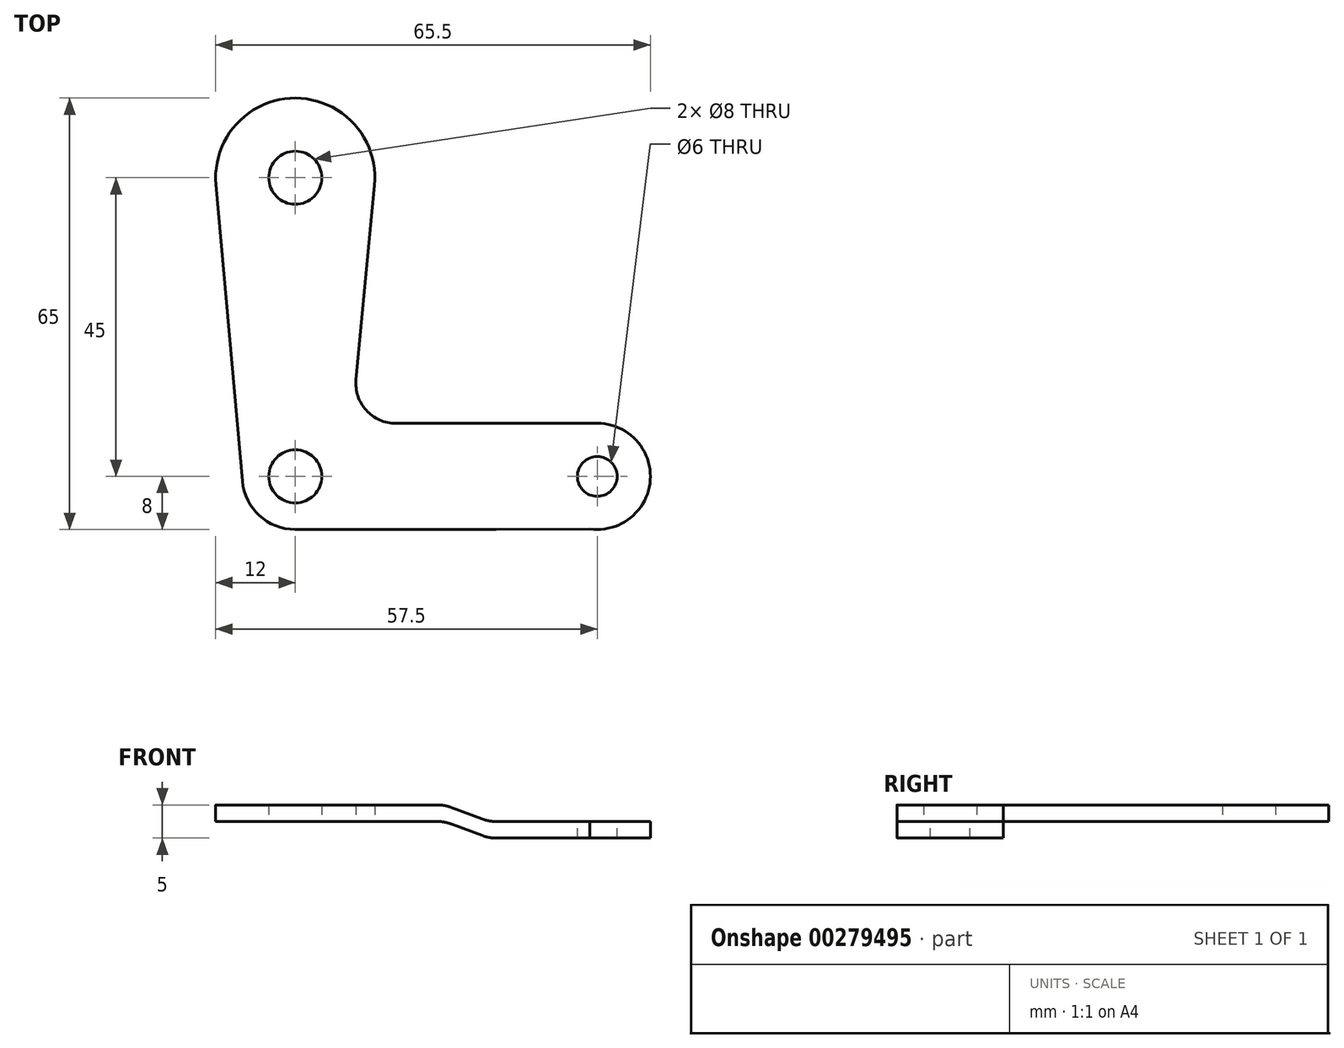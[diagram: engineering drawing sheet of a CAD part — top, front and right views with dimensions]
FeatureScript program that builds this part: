
annotation { "Feature Type Name" : "Feature", "Feature Type Description" : "" }
export const myFeature = defineFeature(function(context is Context, id is Id, definition is map)
    precondition{}
    {
        {
            var Q0;
            Q0=qCreatedBy(makeId("Top.planeOp"),FACE);
            var sketch = newSketch(context, id + "F0", { "sketchPlane" : qUnion([Q0])});
            skCircle(sketch, "E0", {"center": v(0, 0) * mm, "radius": 4 * mm});
            skCircle(sketch, "E1", {"center": v(0, 45) * mm, "radius": 4 * mm});
            skArc(sketch, "E2", {"start": v(11.95, 43.86) * mm, "mid": v(0.04, 57) * mm, "end": v(-11.95, 43.93) * mm});
            skArc(sketch, "E3", {"start": v(-7.97, -0.71) * mm, "mid": v(-5.4, -5.9) * mm, "end": v(0, -8) * mm});
            skLineSegment(sketch, "E4", {"start": v(-11.95, 43.93) * mm, "end": v(-7.97, -0.71) * mm});
            skLineSegment(sketch, "E5", {"start": v(0, -8) * mm, "end": v(22.5, -8) * mm});
            skLineSegment(sketch, "E6", {"start": v(11.95, 43.86) * mm, "end": v(9.16, 14.57) * mm});
            skLineSegment(sketch, "E7", {"start": v(15.13, 8) * mm, "end": v(22.5, 8) * mm});
            skPoint(sketch, "E8.visualSharp", {"position": v(8.53, 8) * mm});
            skArc(sketch, "E8.filletArc", {"start": v(9.16, 14.57) * mm, "mid": v(10.7, 9.96) * mm, "end": v(15.13, 8) * mm});
            skLineSegment(sketch, "E9", {"start": v(22.5, 8) * mm, "end": v(22.5, -8) * mm});
            skSolve(sketch);
        }
        {
            var Q0;
            Q0=qSketchRegion(id+"F0",true);
            extrude(context, id + "F1", {"entities" : qUnion([Q0]), "oppositeDirection" : true, "depth" : 2.5 * mm});
        }
        {
            var Q0;
            Q0=makeQuery(id+"F1.opExtrude","CAP_FACE",FACE,{"disambiguationData":[OSD([sQuery(id+"F0.wireOp",EDGE,"E0"),sQuery(id+"F0.wireOp",EDGE,"E1"),sQuery(id+"F0.wireOp",EDGE,"E2"),sQuery(id+"F0.wireOp",EDGE,"E3"),sQuery(id+"F0.wireOp",EDGE,"E4"),sQuery(id+"F0.wireOp",EDGE,"E5"),sQuery(id+"F0.wireOp",EDGE,"E6"),sQuery(id+"F0.wireOp",EDGE,"E7"),sQuery(id+"F0.wireOp",EDGE,"E8.filletArc"),sQuery(id+"F0.wireOp",EDGE,"E9")])],"isStart":false});
            cPlane(context, id + "F2", {"entities" : qUnion([Q0]), "cplaneType" : CPlaneType.OFFSET, "offset" : 2.5 * mm, "oppositeDirection" : true, "width" : 150 * mm, "height" : 150 * mm});
        }
        {
            var Q0;
            Q0=qCreatedBy(id+"F2.planeOp",FACE);
            var sketch = newSketch(context, id + "F3", { "sketchPlane" : qUnion([Q0])});
            skCircle(sketch, "E10.0", {"center": v(0, 0) * mm, "radius": 4 * mm, "construction": true});
            skLineSegment(sketch, "E11.0", {"start": v(22.5, -8) * mm, "end": v(22.5, 8) * mm, "construction": true});
            skCircle(sketch, "E12", {"center": v(45.5, 0) * mm, "radius": 3 * mm});
            skArc(sketch, "E13", {"start": v(45.5, -8) * mm, "mid": v(53.48, 0.56) * mm, "end": v(44.39, 7.92) * mm});
            skLineSegment(sketch, "E14", {"start": v(29.17, 7.98) * mm, "end": v(46.67, 7.91) * mm});
            skLineSegment(sketch, "E15", {"start": v(29.17, -8) * mm, "end": v(45.5, -8) * mm});
            skLineSegment(sketch, "E16", {"start": v(22.5, 8) * mm, "end": v(22.5, -8) * mm, "construction": true});
            skLineSegment(sketch, "E17", {"start": v(29.17, 7.98) * mm, "end": v(29.17, -8) * mm});
            skSolve(sketch);
        }
        {
            var Q0;
            Q0=qSketchRegion(id+"F3",true);
            extrude(context, id + "F4", {"entities" : qUnion([Q0]), "oppositeDirection" : true, "depth" : 2.5 * mm});
        }
        {
            var Q0;
            Q0=makeQuery(id+"F1.opExtrude","SWEPT_FACE",FACE,{"disambiguationData":[OSD([sQuery(id+"F0.wireOp",EDGE,"E9")])]});
            var Q1;
            Q1=makeQuery(id+"F4.opExtrude","SWEPT_FACE",FACE,{"disambiguationData":[OSD([sQuery(id+"F3.wireOp",EDGE,"E17")])]});
            loft(context, id + "F5", {"sheetProfilesArray" : [{ "sheetProfileEntities" : qUnion([Q0]) }, { "sheetProfileEntities" : qUnion([Q1]) }]});
        }
        {
            var Q0;
            Q0=makeQuery(id+"F1.opExtrude","SWEPT_BODY",BODY,{"disambiguationData":[OSD([sQuery(id+"F0.wireOp",EDGE,"E0"),sQuery(id+"F0.wireOp",EDGE,"E1"),sQuery(id+"F0.wireOp",EDGE,"E2"),sQuery(id+"F0.wireOp",EDGE,"E3"),sQuery(id+"F0.wireOp",EDGE,"E4"),sQuery(id+"F0.wireOp",EDGE,"E5"),sQuery(id+"F0.wireOp",EDGE,"E6"),sQuery(id+"F0.wireOp",EDGE,"E7"),sQuery(id+"F0.wireOp",EDGE,"E8.filletArc"),sQuery(id+"F0.wireOp",EDGE,"E9")])]});
            var Q1;
            Q1=makeQuery(id+"F4.opExtrude","SWEPT_BODY",BODY,{"disambiguationData":[OSD([sQuery(id+"F3.wireOp",EDGE,"E12"),sQuery(id+"F3.wireOp",EDGE,"E13"),sQuery(id+"F3.wireOp",EDGE,"E14"),sQuery(id+"F3.wireOp",EDGE,"E15"),sQuery(id+"F3.wireOp",EDGE,"E17")])]});
            var Q2;
            Q2=makeQuery(id+"F5.opLoft","SWEPT_BODY",BODY,{"disambiguationData":[OSD([sQuery(id+"F0.wireOp",EDGE,"E9"),sQuery(id+"F3.wireOp",EDGE,"E17")])]});
            booleanBodies(context, id + "F6", {"operationType" : BooleanOperationType.UNION, "tools" : qUnion([Q0, Q1, Q2])});
        }
        {
            var Q0;
            {var subQ0=sQuery(id+"F0.wireOp",EDGE,"E9");var subQ1=makeQuery(id+"F1.opExtrude","CAP_EDGE",EDGE,{"disambiguationData":[OSD([subQ0])],"isStart":true});var subQ2=sQuery(id+"F0.wireOp",EDGE,"E7");var subQ3=sQuery(id+"F0.wireOp",EDGE,"E5");Q0=makeQuery(id+"F6.opBoolean","MERGE",EDGE,{"derivedFrom":[subQ1,makeQuery(id+"F5.opLoft","MID_CAP_EDGE",EDGE,{"disambiguationData":[OSD([subQ3,subQ2,subQ0]),TDD([makeQuery(id+"F1.opExtrude","CAP_VERTEX",VERTEX,{"disambiguationData":[OSD([subQ3,subQ0])],"isStart":true}),makeQuery(id+"F1.opExtrude","CAP_VERTEX",VERTEX,{"disambiguationData":[OSD([subQ2,subQ0])],"isStart":true}),subQ1])],"capPos":0.0})]});}
            var Q1;
            {var subQ0=sQuery(id+"F3.wireOp",EDGE,"E17");var subQ1=makeQuery(id+"F4.opExtrude","CAP_EDGE",EDGE,{"disambiguationData":[OSD([subQ0])],"isStart":false});var subQ2=sQuery(id+"F3.wireOp",EDGE,"E15");var subQ3=sQuery(id+"F3.wireOp",EDGE,"E14");Q1=makeQuery(id+"F6.opBoolean","MERGE",EDGE,{"derivedFrom":[subQ1,makeQuery(id+"F5.opLoft","MID_CAP_EDGE",EDGE,{"disambiguationData":[OSD([subQ3,subQ2,subQ0]),TDD([makeQuery(id+"F4.opExtrude","CAP_VERTEX",VERTEX,{"disambiguationData":[OSD([subQ3,subQ0])],"isStart":false}),makeQuery(id+"F4.opExtrude","CAP_VERTEX",VERTEX,{"disambiguationData":[OSD([subQ2,subQ0])],"isStart":false}),subQ1])],"capPos":1.0})]});}
            fillet(context, id + "F7", {"entities" : qUnion([Q0, Q1]), "radius" : 6 * mm, "tangentPropagation" : true, "allowEdgeOverflow" : false});
        }
        {
            var Q0;
            {var subQ0=sQuery(id+"F3.wireOp",EDGE,"E17");var subQ1=makeQuery(id+"F4.opExtrude","CAP_EDGE",EDGE,{"disambiguationData":[OSD([subQ0])],"isStart":true});var subQ2=sQuery(id+"F3.wireOp",EDGE,"E15");var subQ3=sQuery(id+"F3.wireOp",EDGE,"E14");Q0=makeQuery(id+"F6.opBoolean","MERGE",EDGE,{"derivedFrom":[subQ1,makeQuery(id+"F5.opLoft","MID_CAP_EDGE",EDGE,{"disambiguationData":[OSD([subQ3,subQ2,subQ0]),TDD([makeQuery(id+"F4.opExtrude","CAP_VERTEX",VERTEX,{"disambiguationData":[OSD([subQ3,subQ0])],"isStart":true}),makeQuery(id+"F4.opExtrude","CAP_VERTEX",VERTEX,{"disambiguationData":[OSD([subQ2,subQ0])],"isStart":true}),subQ1])],"capPos":1.0})]});}
            var Q1;
            {var subQ0=sQuery(id+"F0.wireOp",EDGE,"E9");var subQ1=makeQuery(id+"F1.opExtrude","CAP_EDGE",EDGE,{"disambiguationData":[OSD([subQ0])],"isStart":false});var subQ2=sQuery(id+"F0.wireOp",EDGE,"E7");var subQ3=sQuery(id+"F0.wireOp",EDGE,"E5");Q1=makeQuery(id+"F6.opBoolean","MERGE",EDGE,{"derivedFrom":[subQ1,makeQuery(id+"F5.opLoft","MID_CAP_EDGE",EDGE,{"disambiguationData":[OSD([subQ3,subQ2,subQ0]),TDD([makeQuery(id+"F1.opExtrude","CAP_VERTEX",VERTEX,{"disambiguationData":[OSD([subQ3,subQ0])],"isStart":false}),makeQuery(id+"F1.opExtrude","CAP_VERTEX",VERTEX,{"disambiguationData":[OSD([subQ2,subQ0])],"isStart":false}),subQ1])],"capPos":0.0})]});}
            fillet(context, id + "F8", {"entities" : qUnion([Q0, Q1]), "radius" : 6 * mm, "tangentPropagation" : true, "allowEdgeOverflow" : false});
        }
        {
            var Q0;
            Q0=makeQuery(id+"F1.opExtrude","SWEPT_BODY",BODY,{"disambiguationData":[OSD([sQuery(id+"F0.wireOp",EDGE,"E0"),sQuery(id+"F0.wireOp",EDGE,"E1"),sQuery(id+"F0.wireOp",EDGE,"E2"),sQuery(id+"F0.wireOp",EDGE,"E3"),sQuery(id+"F0.wireOp",EDGE,"E4"),sQuery(id+"F0.wireOp",EDGE,"E5"),sQuery(id+"F0.wireOp",EDGE,"E6"),sQuery(id+"F0.wireOp",EDGE,"E7"),sQuery(id+"F0.wireOp",EDGE,"E8.filletArc"),sQuery(id+"F0.wireOp",EDGE,"E9")])]});
            var Q1;
            Q1=qCreatedBy(makeId("Top.planeOp"),FACE);
            mirror(context, id + "F9", {"entities" : qUnion([Q0]), "mirrorPlane" : qUnion([Q1])});
        }
        {
            var Q0;
            Q0=makeQuery(id+"F1.opExtrude","SWEPT_BODY",BODY,{"disambiguationData":[OSD([sQuery(id+"F0.wireOp",EDGE,"E0"),sQuery(id+"F0.wireOp",EDGE,"E1"),sQuery(id+"F0.wireOp",EDGE,"E2"),sQuery(id+"F0.wireOp",EDGE,"E3"),sQuery(id+"F0.wireOp",EDGE,"E4"),sQuery(id+"F0.wireOp",EDGE,"E5"),sQuery(id+"F0.wireOp",EDGE,"E6"),sQuery(id+"F0.wireOp",EDGE,"E7"),sQuery(id+"F0.wireOp",EDGE,"E8.filletArc"),sQuery(id+"F0.wireOp",EDGE,"E9")])]});
            deleteBodies(context, id + "F10", {"entities" : qUnion([Q0])});
        }
    });
